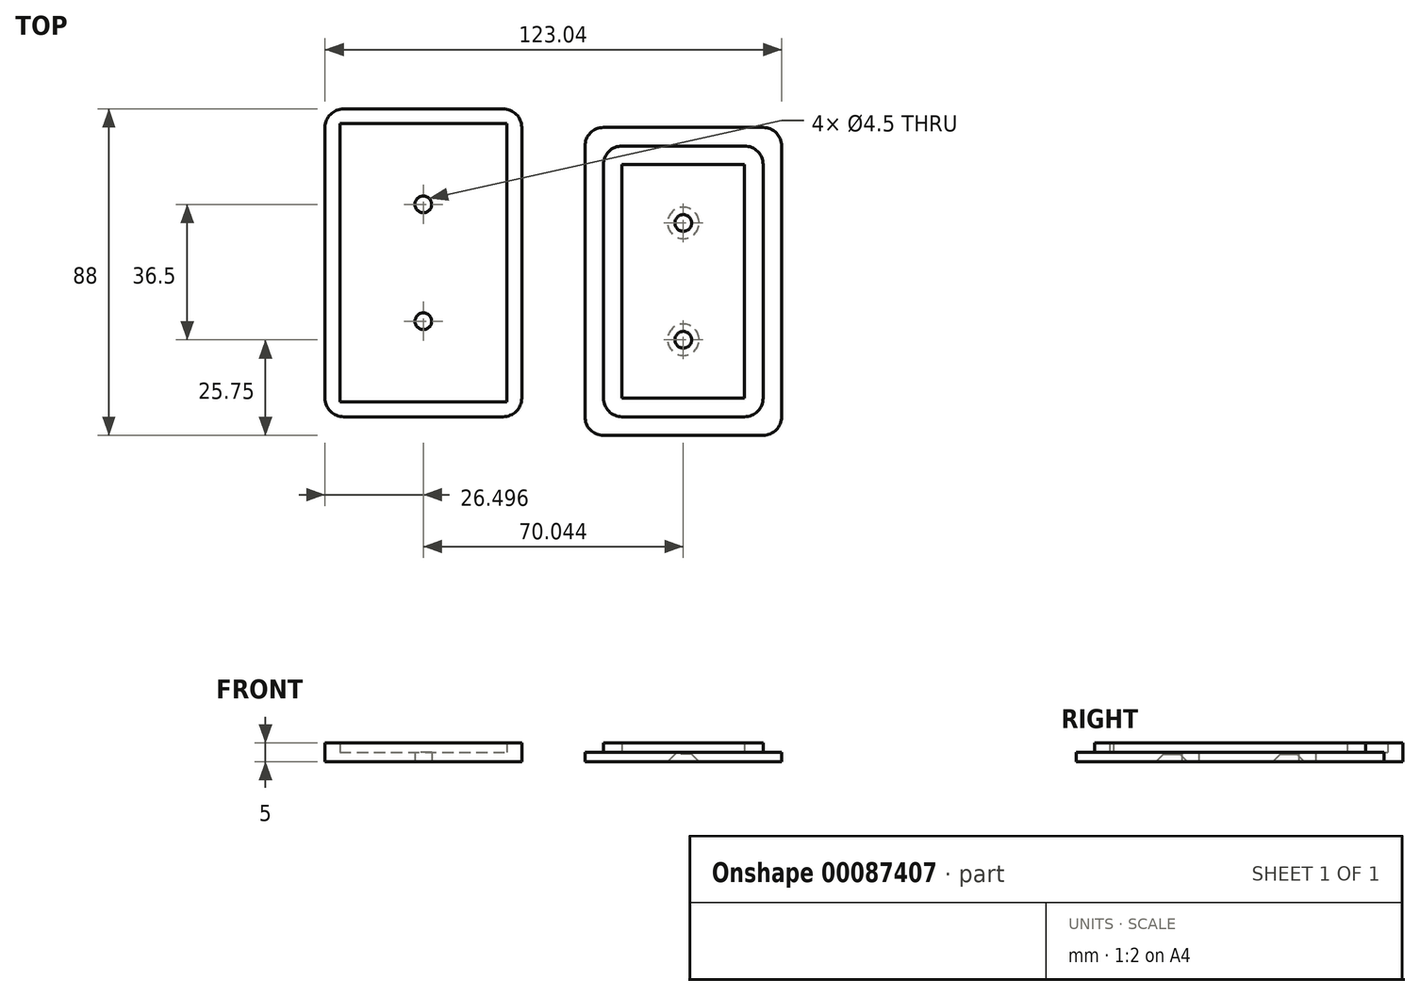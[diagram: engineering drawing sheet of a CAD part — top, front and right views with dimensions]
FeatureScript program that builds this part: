
annotation { "Feature Type Name" : "Feature", "Feature Type Description" : "" }
export const myFeature = defineFeature(function(context is Context, id is Id, definition is map)
    precondition{}
    {
        {
            var Q0;
            Q0=qCreatedBy(makeId("Top.planeOp"),FACE);
            var sketch = newSketch(context, id + "F0", { "sketchPlane" : qUnion([Q0])});
            skLineSegment(sketch, "E0.bottom", {"start": v(0, 0) * mm, "end": v(43, 0) * mm});
            skLineSegment(sketch, "E0.top", {"start": v(0, 73) * mm, "end": v(43, 73) * mm});
            skLineSegment(sketch, "E0.left", {"start": v(0, 0) * mm, "end": v(0, 73) * mm});
            skLineSegment(sketch, "E0.right", {"start": v(43, 0) * mm, "end": v(43, 73) * mm});
            skLineSegment(sketch, "E1.0", {"start": v(-5, 78) * mm, "end": v(48, 78) * mm});
            skLineSegment(sketch, "E1.1", {"start": v(-5, -5) * mm, "end": v(-5, 78) * mm});
            skLineSegment(sketch, "E1.2", {"start": v(-5, -5) * mm, "end": v(48, -5) * mm});
            skLineSegment(sketch, "E1.3", {"start": v(48, -5) * mm, "end": v(48, 78) * mm});
            skLineSegment(sketch, "E2.0", {"start": v(38, 5) * mm, "end": v(38, 68) * mm});
            skLineSegment(sketch, "E2.1", {"start": v(5, 5) * mm, "end": v(38, 5) * mm});
            skLineSegment(sketch, "E2.2", {"start": v(5, 5) * mm, "end": v(5, 68) * mm});
            skLineSegment(sketch, "E2.3", {"start": v(5, 68) * mm, "end": v(38, 68) * mm});
            skCircle(sketch, "E3", {"center": v(21.5, 52.25) * mm, "radius": 2.25 * mm});
            skCircle(sketch, "E4", {"center": v(21.5, 20.75) * mm, "radius": 2.25 * mm});
            skLineSegment(sketch, "E5.bottom", {"start": v(-75.04, 0) * mm, "end": v(-22.04, 0) * mm});
            skLineSegment(sketch, "E5.top", {"start": v(-75.04, 83) * mm, "end": v(-22.04, 83) * mm});
            skLineSegment(sketch, "E5.left", {"start": v(-75.04, 0) * mm, "end": v(-75.04, 83) * mm});
            skLineSegment(sketch, "E5.right", {"start": v(-22.04, 0) * mm, "end": v(-22.04, 83) * mm});
            skLineSegment(sketch, "E6.0", {"start": v(-71.04, 4) * mm, "end": v(-26.04, 4) * mm});
            skLineSegment(sketch, "E6.1", {"start": v(-71.04, 4) * mm, "end": v(-71.04, 79) * mm});
            skLineSegment(sketch, "E6.2", {"start": v(-71.04, 79) * mm, "end": v(-26.04, 79) * mm});
            skLineSegment(sketch, "E6.3", {"start": v(-26.04, 4) * mm, "end": v(-26.04, 79) * mm});
            skCircle(sketch, "E7", {"center": v(-48.54, 57.25) * mm, "radius": 2.25 * mm});
            skCircle(sketch, "E8", {"center": v(-48.54, 25.75) * mm, "radius": 2.25 * mm});
            skSolve(sketch);
        }
        {
            var Q0;
            Q0=makeQuery(id+"F0.imprint","IMPRINT",FACE,{"disambiguationData":[TD([[makeQuery(id+"F0.imprint","IMPRINT",EDGE,{"derivedFrom":sQuery(id+"F0.wireOp",EDGE,"E0.bottom")}),1.0]])]});
            var Q1;
            Q1=makeQuery(id+"F0.imprint","IMPRINT",FACE,{"disambiguationData":[TD([[makeQuery(id+"F0.imprint","IMPRINT",EDGE,{"derivedFrom":sQuery(id+"F0.wireOp",EDGE,"E5.bottom")}),1.0]])]});
            extrude(context, id + "F1", {"entities" : qUnion([Q0, Q1]), "depth" : 5 * mm});
        }
        {
            var Q0;
            Q0=makeQuery(id+"F0.imprint","IMPRINT",FACE,{"disambiguationData":[TD([[makeQuery(id+"F0.imprint","IMPRINT",EDGE,{"derivedFrom":sQuery(id+"F0.wireOp",EDGE,"E0.bottom")}),-1.0]])]});
            var Q1;
            Q1=makeQuery(id+"F0.imprint","IMPRINT",FACE,{"disambiguationData":[TD([[makeQuery(id+"F0.imprint","IMPRINT",EDGE,{"derivedFrom":sQuery(id+"F0.wireOp",EDGE,"E2.0")}),1.0]])]});
            extrude(context, id + "F2", {"entities" : qUnion([Q0, Q1]), "operationType" : NewBodyOperationType.ADD, "depth" : 2.5 * mm});
        }
        {
            var Q0;
            Q0=makeQuery(id+"F2.opExtrude","SWEPT_EDGE",EDGE,{"disambiguationData":[OSD([sQuery(id+"F0.wireOp",EDGE,"E1.0"),sQuery(id+"F0.wireOp",EDGE,"E1.1")])]});
            var Q1;
            Q1=makeQuery(id+"F1.opExtrude","SWEPT_EDGE",EDGE,{"disambiguationData":[OSD([sQuery(id+"F0.wireOp",EDGE,"E0.top"),sQuery(id+"F0.wireOp",EDGE,"E0.left")])]});
            var Q2;
            Q2=makeQuery(id+"F1.opExtrude","SWEPT_EDGE",EDGE,{"disambiguationData":[OSD([sQuery(id+"F0.wireOp",EDGE,"E0.top"),sQuery(id+"F0.wireOp",EDGE,"E0.right")])]});
            var Q3;
            Q3=makeQuery(id+"F2.opExtrude","SWEPT_EDGE",EDGE,{"disambiguationData":[OSD([sQuery(id+"F0.wireOp",EDGE,"E1.0"),sQuery(id+"F0.wireOp",EDGE,"E1.3")])]});
            var Q4;
            Q4=makeQuery(id+"F2.opExtrude","SWEPT_EDGE",EDGE,{"disambiguationData":[OSD([sQuery(id+"F0.wireOp",EDGE,"E1.1"),sQuery(id+"F0.wireOp",EDGE,"E1.2")])]});
            var Q5;
            Q5=makeQuery(id+"F1.opExtrude","SWEPT_EDGE",EDGE,{"disambiguationData":[OSD([sQuery(id+"F0.wireOp",EDGE,"E0.bottom"),sQuery(id+"F0.wireOp",EDGE,"E0.left")])]});
            var Q6;
            Q6=makeQuery(id+"F2.opExtrude","SWEPT_EDGE",EDGE,{"disambiguationData":[OSD([sQuery(id+"F0.wireOp",EDGE,"E1.2"),sQuery(id+"F0.wireOp",EDGE,"E1.3")])]});
            var Q7;
            Q7=makeQuery(id+"F1.opExtrude","SWEPT_EDGE",EDGE,{"disambiguationData":[OSD([sQuery(id+"F0.wireOp",EDGE,"E0.bottom"),sQuery(id+"F0.wireOp",EDGE,"E0.right")])]});
            var Q8;
            Q8=makeQuery(id+"F1.opExtrude","SWEPT_EDGE",EDGE,{"disambiguationData":[OSD([sQuery(id+"F0.wireOp",EDGE,"E5.top"),sQuery(id+"F0.wireOp",EDGE,"E5.left")])]});
            var Q9;
            Q9=makeQuery(id+"F1.opExtrude","SWEPT_EDGE",EDGE,{"disambiguationData":[OSD([sQuery(id+"F0.wireOp",EDGE,"E5.top"),sQuery(id+"F0.wireOp",EDGE,"E5.right")])]});
            var Q10;
            Q10=makeQuery(id+"F1.opExtrude","SWEPT_EDGE",EDGE,{"disambiguationData":[OSD([sQuery(id+"F0.wireOp",EDGE,"E5.bottom"),sQuery(id+"F0.wireOp",EDGE,"E5.left")])]});
            var Q11;
            Q11=makeQuery(id+"F1.opExtrude","SWEPT_EDGE",EDGE,{"disambiguationData":[OSD([sQuery(id+"F0.wireOp",EDGE,"E5.bottom"),sQuery(id+"F0.wireOp",EDGE,"E5.right")])]});
            fillet(context, id + "F3", {"entities" : qUnion([Q0, Q1, Q2, Q3, Q4, Q5, Q6, Q7, Q8, Q9, Q10, Q11]), "radius" : 5 * mm, "tangentPropagation" : true, "allowEdgeOverflow" : false});
        }
        {
            var Q0;
            Q0=makeQuery(id+"F2.opExtrude","CAP_EDGE",EDGE,{"disambiguationData":[OSD([sQuery(id+"F0.wireOp",EDGE,"E3")])],"isStart":true});
            var Q1;
            Q1=makeQuery(id+"F2.opExtrude","CAP_EDGE",EDGE,{"disambiguationData":[OSD([sQuery(id+"F0.wireOp",EDGE,"E4")])],"isStart":true});
            chamfer(context, id + "F4", {"entities" : qUnion([Q0, Q1]), "width" : 2 * mm, "tangentPropagation" : true});
        }
        {
            var Q0;
            Q0=makeQuery(id+"F0.imprint","IMPRINT",FACE,{"disambiguationData":[TD([[makeQuery(id+"F0.imprint","IMPRINT",EDGE,{"derivedFrom":sQuery(id+"F0.wireOp",EDGE,"E6.0")}),1.0]])]});
            extrude(context, id + "F5", {"entities" : qUnion([Q0]), "operationType" : NewBodyOperationType.ADD, "depth" : 2.5 * mm});
        }
    });
